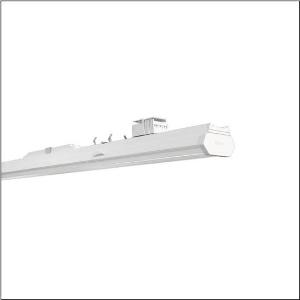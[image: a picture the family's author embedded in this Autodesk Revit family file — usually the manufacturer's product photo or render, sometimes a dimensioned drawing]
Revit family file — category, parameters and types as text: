
# Revit family: licross_r__21_protected_mo_52td12dn4a5g_44fa
name_source: partatom
category: Lighting Fixtures
units: mm (PartAtom-declared; Revit-internal decimal feet)

## family parameters
Cut with Voids When Loaded = No
Host = Face
Light Source = No
Part Type = Normal
Room Calculation Point = No
Round Connector Dimension = Use Diameter
Shared = No

## types (1)
- --- (1 x LED, 10700 lm, 62 W, 4000K)
    Apparent Load = 62 VA
    CIE Flux Codes = 73 92 98 99 100
    Color Rendering = 80
    Color Temperature = 4000K
    Default Elevation = 1800 mm
    Description = Licross® 21 Protected MO, luminaire insert, of sheet steel, galvanised, coil coated, white, length: 1.500mm, width: 90mm, height: 103mm, LED rated luminous flux: 10.700lm, light colour: 840, control gear: DALI 2, with plug, 5-pole, with phase selection, mains connection: 220..240V, AC, 50/60Hz, rated input power: 62W, halogen-free wiring, primary light control with lens, of plastic, primary optical cover: cover, of PMMA, light emission: direct distribution, primary light characteristic: symmetric, protection rating (complete): IP54, insulation class (complete): insulation class I (protective earthing), certification: CE, ENEC, VDE, UKCA, protection symbol: D if used in an environment with non-conductive dust loads with corresponding accessories, impact resistance: IK06, permissible ambient temperature for indoor applications: -25..+35°C, corresponds to IFS (International Featured Standards) requirements for safety and quality in the food industry, reducing of maximum allowable ambient temperature of 5°C with ceiling mounting, LABS conformity tested according to VDMA 24364:2018-05, packaging unit: 1 piece
    Height = 92 mm
    Lamp = 1 x LED
    Lamp Light Flux = 10700 lm
    Lamp Power = 62 W
    Lamp count = 1
    Length = 1500 mm
    Luminous efficacy = 173 lm/W
    Manufacturer = Siteco
    ModVariant = No
    Model = 52TD12DN4A5G
    Mounting Place = Ceiling
    Mounting Type = Pendant
    Number of Poles = 1
    OnlyDefault = Yes
    Power Factor = 1
    Product Name = Licross® 21 Protected MO
    Product group = luminaire insert
    ProductGroupID = 901
    Protection Class = Protection class I
    Protection Degree = IP 54
    RLX_Detail_Level = 1
    RLX_Emergency_Light_Flux = 0 lm
    RLX_Emergency_Type = 0
    RLX_Emergency_Type_DB = No
    RlxData = <blob elided: 24521 chars, md5=7125d3d6>
    Socket = socket
    Standby Power = 0 W
    System Light Flux = 10700 lm
    System Power = 62 W
    Type Comments = factory setting: luminous flux: 100 % | dim-lin: 254 | 418 mA
    Type Image = l_1256148.jpg
    URL = http://relux.com
    VarID = @adj_099105
    Voltage = 0 V
    Weight = 0.00 kg
    Width = 88 mm

## geometry (parser evidence)
native form markers: Blend x4, Sweep x11
no freeform markers — native parametric forms only
